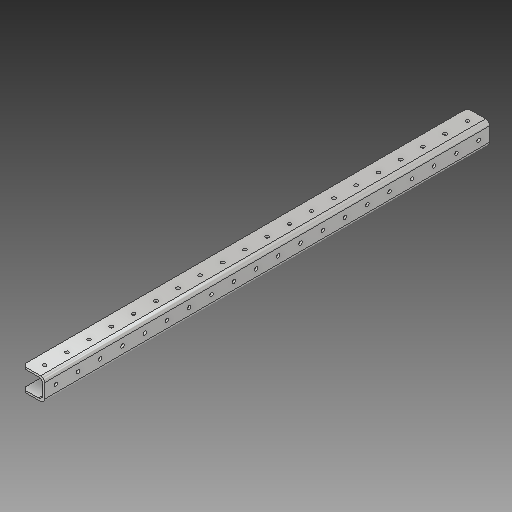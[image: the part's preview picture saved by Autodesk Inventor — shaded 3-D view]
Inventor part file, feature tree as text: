
AUTODESK INVENTOR PART (.ipt)
format: ipt  version: 2018 (Build 220112000, 112)  size: 217,600 bytes
history: native  units: in
note: dims shown in document units (in); Inventor stores cm internally (conversion verified against a paired STEP export)
features: sketch x4, other x3, hole x3, pattern_linear x3, projected_geometry x2, extrude x1, chamfer x1, fillet x1
ambient origin geometry x8: Origin, YZ Plane, XZ Plane, XY Plane, X Axis, Y Axis, Z Axis, Center Point
bodies: Solid1 (feature_tree)
feature tree (18):
  other  "Table"
  other  "channel-1x1x1"
  other  "channel-1x2x1"
  extrude  "Extrusion1"  Depth=1.0in
  hole  "Hole1"  [1 undecoded]
  hole  "Hole2"  [1 undecoded]
  hole  "Hole3"  [1 undecoded]
  pattern_linear  "Rectangular Pattern1"  Spacing1=0.5in  [1 undecoded]
  pattern_linear  "Rectangular Pattern2"  Spacing1=0.5in  [1 undecoded]
  pattern_linear  "Rectangular Pattern3"  Count1=21  [1 undecoded]
  chamfer  "Chamfer1"  Distance=1.0in
  fillet  "Fillet1"  Radius=8.2677in
  sketch  "Sketch1"  dims[d4=0.0in d5=1.0in]
  sketch  "Sketch2"  dims[d7=0.5in d8=0.5in]
  projected_geometry  "Projected Loop1"
  sketch  "Sketch3"  dims[d9=0.161in d10=0.75in d11=0.119in d12=0.25in d13=0.5635in d14=1.0in d15=0.8108in d17=1.0in]
  projected_geometry  "Projected Loop2"
  sketch  "Sketch4"  dims[d18=0.5in d19=0.161in d20=0.75in d21=0.119in d22=0.25in d23=0.5635in d24=1.0in d25=0.8108in d26=0.5in d27=0.5in d28=0.5in d29=0.161in d30=0.75in d31=0.119in d32=0.25in d33=0.5635in d34=1.0in d35=0.8108in d36=8.2677in d38=1.0in d39=8.2677in d41=1.0in d42=8.2677in d44=1.0in d45=0.125in d46=0.125in d47=45.0deg d48=0.18in]
note: 6 required parameter values undecoded (feature->parameter linkage not recoverable at this tier; creation-order binding heuristic only, values carry confidence <= 0.55)
